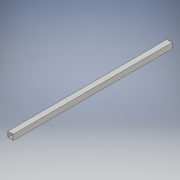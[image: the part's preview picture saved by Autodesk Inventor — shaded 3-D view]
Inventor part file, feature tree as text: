
AUTODESK INVENTOR PART (.ipt)
format: ipt  version: 2018 (Build 220112000, 112)  size: 112,640 bytes
history: native  units: in
note: dims shown in document units (in); Inventor stores cm internally (conversion verified against a paired STEP export)
features: extrude x3, sketch x3
ambient origin geometry x8: Origin, YZ Plane, XZ Plane, XY Plane, X Axis, Y Axis, Z Axis, Center Point
bodies: Solid1 (feature_tree)
feature tree (6):
  extrude  "Extrusion1"  Depth=1.0in
  extrude  "Extrusion2"  Depth=0.125in
  extrude  "Extrusion3"  Depth=0.75in
  sketch  "Sketch1"  dims[d0=31.0in d1=1.0in]
  sketch  "Sketch2"  dims[d2=1.0in d3=0.0in d4=0.125in]
  sketch  "Sketch3"  dims[d5=0.125in d6=0.75in d7=0.75in d8=31.0in d9=0.0in d10=2.0in d11=0.0in]
